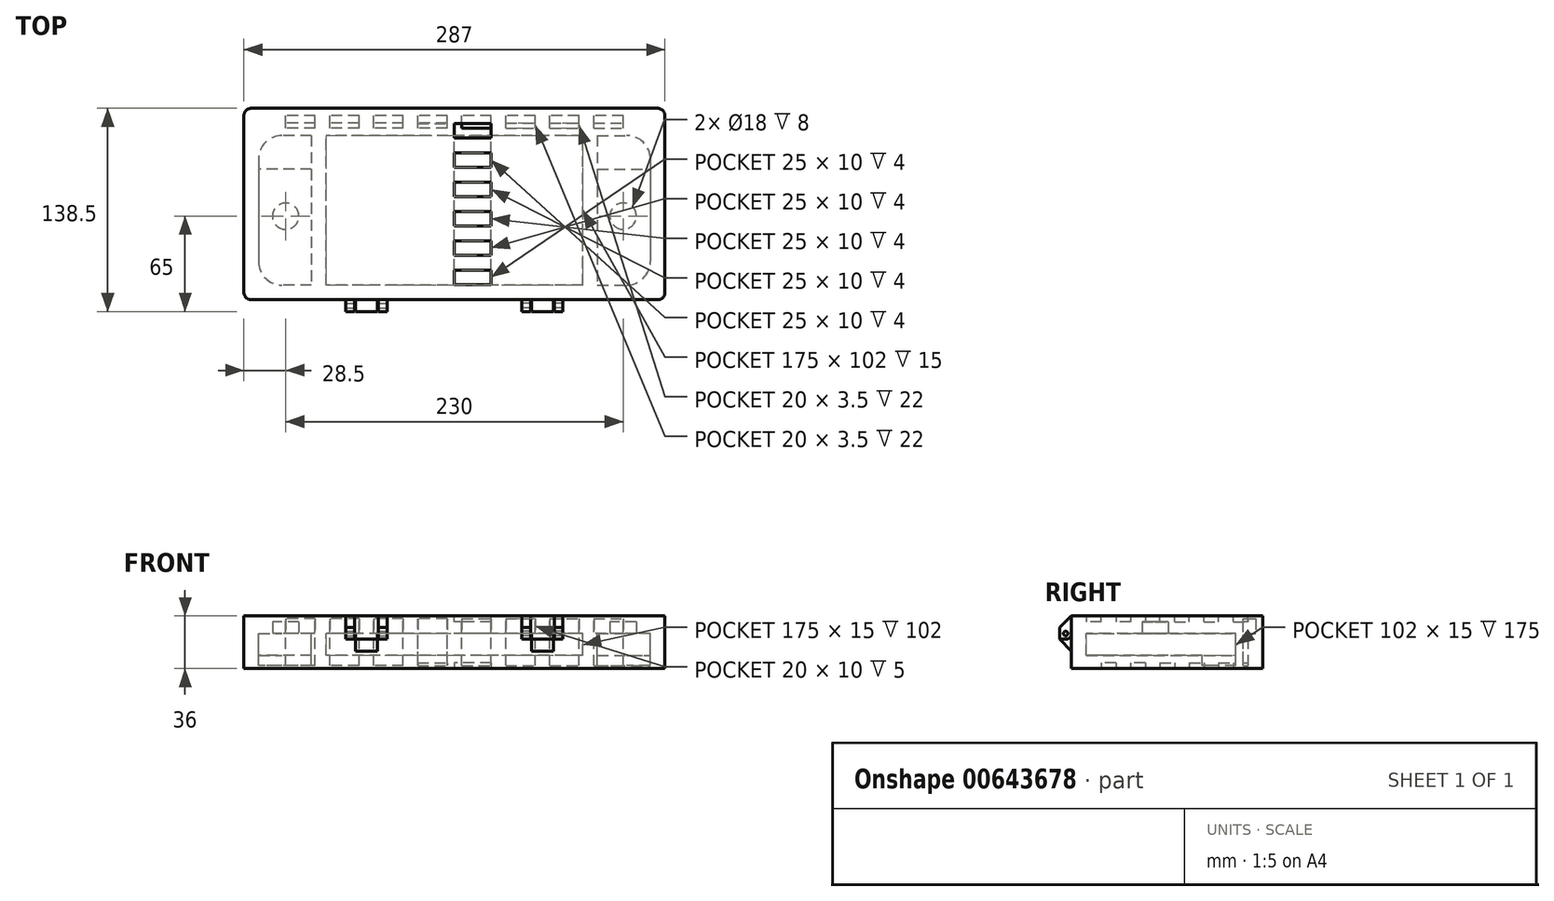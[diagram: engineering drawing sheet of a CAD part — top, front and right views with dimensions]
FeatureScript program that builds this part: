
annotation { "Feature Type Name" : "Feature", "Feature Type Description" : "" }
export const myFeature = defineFeature(function(context is Context, id is Id, definition is map)
    precondition{}
    {
        {
            var Q0;
            Q0=qCreatedBy(makeId("Right.planeOp"),FACE);
            cPlane(context, id + "F0", {"entities" : qUnion([Q0]), "cplaneType" : CPlaneType.OFFSET, "offset" : 60 * mm, "oppositeDirection" : true, "width" : 150 * mm, "height" : 150 * mm});
        }
        {
            var Q0;
            Q0=qCreatedBy(makeId("Right.planeOp"),FACE);
            cPlane(context, id + "F1", {"entities" : qUnion([Q0]), "cplaneType" : CPlaneType.OFFSET, "offset" : 60 * mm, "width" : 150 * mm, "height" : 150 * mm});
        }
        {
            var Q0;
            Q0=qCreatedBy(makeId("Top.planeOp"),FACE);
            var sketch = newSketch(context, id + "F2", { "sketchPlane" : qUnion([Q0])});
            skLineSegment(sketch, "E0.bottom", {"start": v(87.5, -51) * mm, "end": v(-87.5, -51) * mm});
            skLineSegment(sketch, "E0.top", {"start": v(87.5, 51) * mm, "end": v(-87.5, 51) * mm});
            skLineSegment(sketch, "E0.left", {"start": v(87.5, -51) * mm, "end": v(87.5, 51) * mm});
            skLineSegment(sketch, "E0.right", {"start": v(-87.5, -51) * mm, "end": v(-87.5, 51) * mm});
            skPoint(sketch, "E0.middle", {"position": v(0, 0) * mm});
            skLineSegment(sketch, "E1.bottom", {"start": v(97.5, 51) * mm, "end": v(117.5, 51) * mm});
            skLineSegment(sketch, "E1.top", {"start": v(97.5, -51) * mm, "end": v(117.5, -51) * mm});
            skLineSegment(sketch, "E1.left", {"start": v(97.5, 51) * mm, "end": v(97.5, -51) * mm});
            skLineSegment(sketch, "E1.right", {"start": v(133.5, 35) * mm, "end": v(133.5, -35) * mm});
            skPoint(sketch, "E2.visualSharp", {"position": v(133.5, 51) * mm});
            skArc(sketch, "E2.filletArc", {"start": v(133.5, 35) * mm, "mid": v(128.81, 46.31) * mm, "end": v(117.5, 51) * mm});
            skPoint(sketch, "E3.visualSharp", {"position": v(133.5, -51) * mm});
            skArc(sketch, "E3.filletArc", {"start": v(117.5, -51) * mm, "mid": v(128.81, -46.31) * mm, "end": v(133.5, -35) * mm});
            skLineSegment(sketch, "E4.bottom", {"start": v(-97.5, 51) * mm, "end": v(-117.5, 51) * mm});
            skLineSegment(sketch, "E4.top", {"start": v(-97.5, -51) * mm, "end": v(-117.5, -51) * mm});
            skLineSegment(sketch, "E4.left", {"start": v(-97.5, 51) * mm, "end": v(-97.5, -51) * mm});
            skLineSegment(sketch, "E4.right", {"start": v(-133.5, 35) * mm, "end": v(-133.5, -35) * mm});
            skPoint(sketch, "E5.visualSharp", {"position": v(-133.5, 51) * mm});
            skArc(sketch, "E5.filletArc", {"start": v(-117.5, 51) * mm, "mid": v(-128.81, 46.31) * mm, "end": v(-133.5, 35) * mm});
            skPoint(sketch, "E6.visualSharp", {"position": v(-133.5, -51) * mm});
            skArc(sketch, "E6.filletArc", {"start": v(-133.5, -35) * mm, "mid": v(-128.81, -46.31) * mm, "end": v(-117.5, -51) * mm});
            skLineSegment(sketch, "E7.bottom", {"start": v(-143.5, 69.5) * mm, "end": v(143.5, 69.5) * mm, "construction": true});
            skLineSegment(sketch, "E7.top", {"start": v(-143.5, -61) * mm, "end": v(143.5, -61) * mm, "construction": true});
            skLineSegment(sketch, "E7.left", {"start": v(-143.5, 69.5) * mm, "end": v(-143.5, -61) * mm, "construction": true});
            skLineSegment(sketch, "E7.right", {"start": v(143.5, 69.5) * mm, "end": v(143.5, -61) * mm, "construction": true});
            skLineSegment(sketch, "E8.bottom", {"start": v(5, 56) * mm, "end": v(25, 56) * mm});
            skLineSegment(sketch, "E8.top", {"start": v(5, 59.5) * mm, "end": v(25, 59.5) * mm});
            skLineSegment(sketch, "E8.left", {"start": v(5, 56) * mm, "end": v(5, 59.5) * mm});
            skLineSegment(sketch, "E8.right", {"start": v(25, 56) * mm, "end": v(25, 59.5) * mm});
            skLineSegment(sketch, "E9", {"start": v(0, -61) * mm, "end": v(0, 69.5) * mm, "construction": true});
            skLineSegment(sketch, "E10.bottom", {"start": v(35, 56) * mm, "end": v(55, 56) * mm});
            skLineSegment(sketch, "E10.top", {"start": v(35, 59.5) * mm, "end": v(55, 59.5) * mm});
            skLineSegment(sketch, "E10.left", {"start": v(35, 56) * mm, "end": v(35, 59.5) * mm});
            skLineSegment(sketch, "E10.right", {"start": v(55, 56) * mm, "end": v(55, 59.5) * mm});
            skLineSegment(sketch, "E11.bottom", {"start": v(65, 56) * mm, "end": v(85, 56) * mm});
            skLineSegment(sketch, "E11.top", {"start": v(65, 59.5) * mm, "end": v(85, 59.5) * mm});
            skLineSegment(sketch, "E11.left", {"start": v(65, 56) * mm, "end": v(65, 59.5) * mm});
            skLineSegment(sketch, "E11.right", {"start": v(85, 56) * mm, "end": v(85, 59.5) * mm});
            skLineSegment(sketch, "E12.bottom", {"start": v(95, 56) * mm, "end": v(115, 56) * mm});
            skLineSegment(sketch, "E12.top", {"start": v(95, 59.5) * mm, "end": v(115, 59.5) * mm});
            skLineSegment(sketch, "E12.left", {"start": v(95, 56) * mm, "end": v(95, 59.5) * mm});
            skLineSegment(sketch, "E12.right", {"start": v(115, 56) * mm, "end": v(115, 59.5) * mm});
            skLineSegment(sketch, "E13.bottom", {"start": v(-5, 56) * mm, "end": v(-25, 56) * mm});
            skLineSegment(sketch, "E13.top", {"start": v(-5, 59.5) * mm, "end": v(-25, 59.5) * mm});
            skLineSegment(sketch, "E13.left", {"start": v(-5, 56) * mm, "end": v(-5, 59.5) * mm});
            skLineSegment(sketch, "E13.right", {"start": v(-25, 56) * mm, "end": v(-25, 59.5) * mm});
            skLineSegment(sketch, "E14.bottom", {"start": v(-35, 56) * mm, "end": v(-55, 56) * mm});
            skLineSegment(sketch, "E14.top", {"start": v(-35, 59.5) * mm, "end": v(-55, 59.5) * mm});
            skLineSegment(sketch, "E14.left", {"start": v(-35, 56) * mm, "end": v(-35, 59.5) * mm});
            skLineSegment(sketch, "E14.right", {"start": v(-55, 56) * mm, "end": v(-55, 59.5) * mm});
            skLineSegment(sketch, "E15.bottom", {"start": v(-65, 56) * mm, "end": v(-85, 56) * mm});
            skLineSegment(sketch, "E15.top", {"start": v(-65, 59.5) * mm, "end": v(-85, 59.5) * mm});
            skLineSegment(sketch, "E15.left", {"start": v(-65, 56) * mm, "end": v(-65, 59.5) * mm});
            skLineSegment(sketch, "E15.right", {"start": v(-85, 56) * mm, "end": v(-85, 59.5) * mm});
            skLineSegment(sketch, "E16.bottom", {"start": v(-95, 56) * mm, "end": v(-115, 56) * mm});
            skLineSegment(sketch, "E16.top", {"start": v(-95, 59.5) * mm, "end": v(-115, 59.5) * mm});
            skLineSegment(sketch, "E16.left", {"start": v(-95, 56) * mm, "end": v(-95, 59.5) * mm});
            skLineSegment(sketch, "E16.right", {"start": v(-115, 56) * mm, "end": v(-115, 59.5) * mm});
            skLineSegment(sketch, "E17", {"start": v(97.5, 28) * mm, "end": v(133.5, 28) * mm});
            skLineSegment(sketch, "E18", {"start": v(-97.5, 28) * mm, "end": v(-133.5, 28) * mm});
            skPoint(sketch, "E18.startSnap0", {"position": v(115.5, 28) * mm});
            skCircle(sketch, "E19", {"center": v(115, -4) * mm, "radius": 9 * mm});
            skCircle(sketch, "E20", {"center": v(-115, -4) * mm, "radius": 9 * mm});
            skLineSegment(sketch, "E21.bottom", {"start": v(115, 59.5) * mm, "end": v(95, 59.5) * mm});
            skLineSegment(sketch, "E21.top", {"start": v(115, 64.5) * mm, "end": v(95, 64.5) * mm});
            skLineSegment(sketch, "E21.left", {"start": v(115, 59.5) * mm, "end": v(115, 64.5) * mm});
            skLineSegment(sketch, "E21.right", {"start": v(95, 59.5) * mm, "end": v(95, 64.5) * mm});
            skLineSegment(sketch, "E22.bottom", {"start": v(85, 59.5) * mm, "end": v(65, 59.5) * mm});
            skLineSegment(sketch, "E22.top", {"start": v(85, 64.5) * mm, "end": v(65, 64.5) * mm});
            skLineSegment(sketch, "E22.left", {"start": v(85, 59.5) * mm, "end": v(85, 64.5) * mm});
            skLineSegment(sketch, "E22.right", {"start": v(65, 59.5) * mm, "end": v(65, 64.5) * mm});
            skLineSegment(sketch, "E23.bottom", {"start": v(55, 59.5) * mm, "end": v(35, 59.5) * mm});
            skLineSegment(sketch, "E23.top", {"start": v(55, 64.5) * mm, "end": v(35, 64.5) * mm});
            skLineSegment(sketch, "E23.left", {"start": v(55, 59.5) * mm, "end": v(55, 64.5) * mm});
            skLineSegment(sketch, "E23.right", {"start": v(35, 59.5) * mm, "end": v(35, 64.5) * mm});
            skLineSegment(sketch, "E24.bottom", {"start": v(25, 59.5) * mm, "end": v(5, 59.5) * mm});
            skLineSegment(sketch, "E24.top", {"start": v(25, 64.5) * mm, "end": v(5, 64.5) * mm});
            skLineSegment(sketch, "E24.left", {"start": v(25, 59.5) * mm, "end": v(25, 64.5) * mm});
            skLineSegment(sketch, "E24.right", {"start": v(5, 59.5) * mm, "end": v(5, 64.5) * mm});
            skLineSegment(sketch, "E25.top", {"start": v(-5, 64.5) * mm, "end": v(-25, 64.5) * mm});
            skLineSegment(sketch, "E25.left", {"start": v(-5, 59.5) * mm, "end": v(-5, 64.5) * mm});
            skLineSegment(sketch, "E25.right", {"start": v(-25, 59.5) * mm, "end": v(-25, 64.5) * mm});
            skLineSegment(sketch, "E26.top", {"start": v(-35, 64.5) * mm, "end": v(-55, 64.5) * mm});
            skLineSegment(sketch, "E26.left", {"start": v(-35, 59.5) * mm, "end": v(-35, 64.5) * mm});
            skLineSegment(sketch, "E26.right", {"start": v(-55, 59.5) * mm, "end": v(-55, 64.5) * mm});
            skLineSegment(sketch, "E27.top", {"start": v(-65, 64.5) * mm, "end": v(-85, 64.5) * mm});
            skLineSegment(sketch, "E27.left", {"start": v(-65, 59.5) * mm, "end": v(-65, 64.5) * mm});
            skLineSegment(sketch, "E27.right", {"start": v(-85, 59.5) * mm, "end": v(-85, 64.5) * mm});
            skLineSegment(sketch, "E28.top", {"start": v(-95, 64.5) * mm, "end": v(-115, 64.5) * mm});
            skLineSegment(sketch, "E28.left", {"start": v(-95, 59.5) * mm, "end": v(-95, 64.5) * mm});
            skLineSegment(sketch, "E28.right", {"start": v(-115, 59.5) * mm, "end": v(-115, 64.5) * mm});
            skSolve(sketch);
        }
        {
            var Q0;
            Q0=qCreatedBy(makeId("Top.planeOp"),FACE);
            var sketch = newSketch(context, id + "F3", { "sketchPlane" : qUnion([Q0])});
            skLineSegment(sketch, "E29.bottom", {"start": v(138.5, -61) * mm, "end": v(-138.5, -61) * mm});
            skLineSegment(sketch, "E29.top", {"start": v(138.5, 69.5) * mm, "end": v(-138.5, 69.5) * mm});
            skLineSegment(sketch, "E29.left", {"start": v(143.5, -56) * mm, "end": v(143.5, 64.5) * mm});
            skLineSegment(sketch, "E29.right", {"start": v(-143.5, -56) * mm, "end": v(-143.5, 64.5) * mm});
            skPoint(sketch, "E29.middle", {"position": v(0, 0) * mm});
            skLineSegment(sketch, "E30", {"start": v(0, 69.5) * mm, "end": v(0, -61) * mm});
            skPoint(sketch, "E31.visualSharp", {"position": v(-143.5, 69.5) * mm});
            skArc(sketch, "E31.filletArc", {"start": v(-138.5, 69.5) * mm, "mid": v(-142.04, 68.04) * mm, "end": v(-143.5, 64.5) * mm});
            skPoint(sketch, "E32.visualSharp", {"position": v(-143.5, -61) * mm});
            skArc(sketch, "E32.filletArc", {"start": v(-143.5, -56) * mm, "mid": v(-142.04, -59.54) * mm, "end": v(-138.5, -61) * mm});
            skPoint(sketch, "E33.visualSharp", {"position": v(143.5, -61) * mm});
            skArc(sketch, "E33.filletArc", {"start": v(138.5, -61) * mm, "mid": v(142.04, -59.54) * mm, "end": v(143.5, -56) * mm});
            skPoint(sketch, "E34.visualSharp", {"position": v(143.5, 69.5) * mm});
            skArc(sketch, "E34.filletArc", {"start": v(143.5, 64.5) * mm, "mid": v(142.04, 68.04) * mm, "end": v(138.5, 69.5) * mm});
            skSolve(sketch);
        }
        {
            var Q0;
            Q0=qCreatedBy(id+"F0.planeOp",FACE);
            var sketch = newSketch(context, id + "F4", { "sketchPlane" : qUnion([Q0])});
            skLineSegment(sketch, "E35", {"start": v(-61, 65.25) * mm, "end": v(-61, -65.25) * mm, "construction": true});
            skLineSegment(sketch, "E36", {"start": v(-61, 0) * mm, "end": v(-69, 0) * mm});
            skLineSegment(sketch, "E37", {"start": v(-69, 0) * mm, "end": v(-69, -4) * mm});
            skLineSegment(sketch, "E38", {"start": v(-61, 0) * mm, "end": v(-61, -12) * mm});
            skLineSegment(sketch, "E39", {"start": v(-61, -12) * mm, "end": v(-69, -4) * mm});
            skLineSegment(sketch, "E40", {"start": v(-61, 0) * mm, "end": v(-61, 12) * mm});
            skLineSegment(sketch, "E41", {"start": v(-61, 12) * mm, "end": v(-69, 4) * mm});
            skLineSegment(sketch, "E42", {"start": v(-69, 4) * mm, "end": v(-69, 0) * mm});
            skLineSegment(sketch, "E43", {"start": v(-69, 4) * mm, "end": v(-61, 4) * mm});
            skLineSegment(sketch, "E44", {"start": v(-69, -4) * mm, "end": v(-61, -4) * mm});
            skCircle(sketch, "E45", {"center": v(-65, 0) * mm, "radius": 1.5 * mm});
            skPoint(sketch, "E46", {"position": v(-65, -4) * mm});
            skArc(sketch, "E47", {"start": v(-65, 4) * mm, "mid": v(-61, 0) * mm, "end": v(-65, -4) * mm});
            skSolve(sketch);
        }
        {
            var Q0;
            Q0=qCreatedBy(id+"F1.planeOp",FACE);
            var sketch = newSketch(context, id + "F5", { "sketchPlane" : qUnion([Q0])});
            skLineSegment(sketch, "E48", {"start": v(-61, 62.75) * mm, "end": v(-61, -62.75) * mm, "construction": true});
            skLineSegment(sketch, "E49", {"start": v(-61, 0) * mm, "end": v(-69, 0) * mm});
            skLineSegment(sketch, "E50", {"start": v(-69, 0) * mm, "end": v(-69, -4) * mm});
            skLineSegment(sketch, "E51", {"start": v(-61, 0) * mm, "end": v(-61, -12) * mm});
            skLineSegment(sketch, "E52", {"start": v(-61, -12) * mm, "end": v(-69, -4) * mm});
            skLineSegment(sketch, "E53", {"start": v(-61, 0) * mm, "end": v(-61, 12) * mm});
            skLineSegment(sketch, "E54", {"start": v(-61, 12) * mm, "end": v(-69, 4) * mm});
            skLineSegment(sketch, "E55", {"start": v(-69, 4) * mm, "end": v(-69, 0) * mm});
            skLineSegment(sketch, "E56", {"start": v(-69, 4) * mm, "end": v(-61, 4) * mm});
            skLineSegment(sketch, "E57", {"start": v(-69, -4) * mm, "end": v(-61, -4) * mm});
            skCircle(sketch, "E58", {"center": v(-65, 0) * mm, "radius": 1.5 * mm});
            skArc(sketch, "E59", {"start": v(-65, 4) * mm, "mid": v(-61, 0) * mm, "end": v(-65, -4) * mm});
            skSolve(sketch);
        }
        {
            var Q0;
            {var subQ2=sQuery(id+"F3.wireOp",EDGE,"E29.right");Q0=makeQuery(id+"F3.imprint","IMPRINT",FACE,{"disambiguationData":[TD([[makeQuery(id+"F3.imprint","IMPRINT",EDGE,{"derivedFrom":subQ2}),-1.0]])]});}
            extrude(context, id + "F6", {"entities" : qUnion([Q0]), "oppositeDirection" : true, "depth" : 24 * mm, "offsetDistance" : 25 * mm});
        }
        {
            var Q0;
            {var subQ2=sQuery(id+"F3.wireOp",EDGE,"E29.left");Q0=makeQuery(id+"F3.imprint","IMPRINT",FACE,{"disambiguationData":[TD([[makeQuery(id+"F3.imprint","IMPRINT",EDGE,{"derivedFrom":subQ2}),1.0]])]});}
            extrude(context, id + "F7", {"entities" : qUnion([Q0]), "oppositeDirection" : true, "depth" : 24 * mm, "offsetDistance" : 25 * mm});
        }
        {
            var Q0;
            Q0=makeQuery(id+"F3.imprint","IMPRINT",FACE,{"disambiguationData":[TD([[makeQuery(id+"F3.imprint","IMPRINT",EDGE,{"derivedFrom":sQuery(id+"F3.wireOp",EDGE,"E29.right")}),-1.0]])]});
            extrude(context, id + "F8", {"entities" : qUnion([Q0]), "depth" : 12 * mm, "offsetDistance" : 25 * mm});
        }
        {
            var Q0;
            Q0=makeQuery(id+"F3.imprint","IMPRINT",FACE,{"disambiguationData":[TD([[makeQuery(id+"F3.imprint","IMPRINT",EDGE,{"derivedFrom":sQuery(id+"F3.wireOp",EDGE,"E29.left")}),1.0]])]});
            extrude(context, id + "F9", {"entities" : qUnion([Q0]), "depth" : 12 * mm, "offsetDistance" : 25 * mm});
        }
        {
            var Q0;
            {var subQ4=sQuery(id+"F2.wireOp",EDGE,"E4.top");Q0=makeQuery(id+"F2.imprint","IMPRINT",FACE,{"disambiguationData":[TD([[makeQuery(id+"F2.imprint","IMPRINT",EDGE,{"derivedFrom":subQ4}),-1.0]])]});}
            var Q1;
            {var subQ4=sQuery(id+"F2.wireOp",EDGE,"E1.top");Q1=makeQuery(id+"F2.imprint","IMPRINT",FACE,{"disambiguationData":[TD([[makeQuery(id+"F2.imprint","IMPRINT",EDGE,{"derivedFrom":subQ4}),1.0]])]});}
            var Q2;
            Q2=makeQuery(id+"F2.imprint","IMPRINT",FACE,{"disambiguationData":[TD([[makeQuery(id+"F2.imprint","IMPRINT",EDGE,{"derivedFrom":sQuery(id+"F2.wireOp",EDGE,"E0.bottom")}),-1.0]])]});
            var Q3;
            Q3=makeQuery(id+"F2.imprint","IMPRINT",FACE,{"disambiguationData":[TD([[makeQuery(id+"F2.imprint","IMPRINT",EDGE,{"derivedFrom":sQuery(id+"F2.wireOp",EDGE,"E20")}),1.0]])]});
            var Q4;
            Q4=makeQuery(id+"F2.imprint","IMPRINT",FACE,{"disambiguationData":[TD([[makeQuery(id+"F2.imprint","IMPRINT",EDGE,{"derivedFrom":sQuery(id+"F2.wireOp",EDGE,"E19")}),1.0]])]});
            extrude(context, id + "F10", {"entities" : qUnion([Q0, Q1, Q2, Q3, Q4]), "operationType" : NewBodyOperationType.REMOVE, "oppositeDirection" : true, "depth" : 15 * mm, "offsetDistance" : 25 * mm});
        }
        {
            var Q0;
            {var subQ2=sQuery(id+"F2.wireOp",EDGE,"E4.bottom");Q0=makeQuery(id+"F2.imprint","IMPRINT",FACE,{"disambiguationData":[TD([[makeQuery(id+"F2.imprint","IMPRINT",EDGE,{"derivedFrom":subQ2}),1.0]])]});}
            var Q1;
            {var subQ2=sQuery(id+"F2.wireOp",EDGE,"E1.bottom");Q1=makeQuery(id+"F2.imprint","IMPRINT",FACE,{"disambiguationData":[TD([[makeQuery(id+"F2.imprint","IMPRINT",EDGE,{"derivedFrom":subQ2}),-1.0]])]});}
            var Q2;
            Q2=makeQuery(id+"F2.imprint","IMPRINT",FACE,{"disambiguationData":[TD([[makeQuery(id+"F2.imprint","IMPRINT",EDGE,{"derivedFrom":sQuery(id+"F2.wireOp",EDGE,"E16.bottom")}),-1.0]])]});
            var Q3;
            Q3=makeQuery(id+"F2.imprint","IMPRINT",FACE,{"disambiguationData":[TD([[makeQuery(id+"F2.imprint","IMPRINT",EDGE,{"derivedFrom":sQuery(id+"F2.wireOp",EDGE,"E15.bottom")}),-1.0]])]});
            var Q4;
            Q4=makeQuery(id+"F2.imprint","IMPRINT",FACE,{"disambiguationData":[TD([[makeQuery(id+"F2.imprint","IMPRINT",EDGE,{"derivedFrom":sQuery(id+"F2.wireOp",EDGE,"E14.bottom")}),-1.0]])]});
            var Q5;
            Q5=makeQuery(id+"F2.imprint","IMPRINT",FACE,{"disambiguationData":[TD([[makeQuery(id+"F2.imprint","IMPRINT",EDGE,{"derivedFrom":sQuery(id+"F2.wireOp",EDGE,"E13.bottom")}),-1.0]])]});
            var Q6;
            Q6=makeQuery(id+"F2.imprint","IMPRINT",FACE,{"disambiguationData":[TD([[makeQuery(id+"F2.imprint","IMPRINT",EDGE,{"derivedFrom":sQuery(id+"F2.wireOp",EDGE,"E8.bottom")}),1.0]])]});
            var Q7;
            Q7=makeQuery(id+"F2.imprint","IMPRINT",FACE,{"disambiguationData":[TD([[makeQuery(id+"F2.imprint","IMPRINT",EDGE,{"derivedFrom":sQuery(id+"F2.wireOp",EDGE,"E10.bottom")}),1.0]])]});
            var Q8;
            Q8=makeQuery(id+"F2.imprint","IMPRINT",FACE,{"disambiguationData":[TD([[makeQuery(id+"F2.imprint","IMPRINT",EDGE,{"derivedFrom":sQuery(id+"F2.wireOp",EDGE,"E11.bottom")}),1.0]])]});
            var Q9;
            Q9=makeQuery(id+"F2.imprint","IMPRINT",FACE,{"disambiguationData":[TD([[makeQuery(id+"F2.imprint","IMPRINT",EDGE,{"derivedFrom":sQuery(id+"F2.wireOp",EDGE,"E12.bottom")}),1.0]])]});
            extrude(context, id + "F11", {"entities" : qUnion([Q0, Q1, Q2, Q3, Q4, Q5, Q6, Q7, Q8, Q9]), "operationType" : NewBodyOperationType.REMOVE, "oppositeDirection" : true, "depth" : 22 * mm, "offsetDistance" : 25 * mm});
        }
        {
            var Q0;
            Q0=makeQuery(id+"F2.imprint","IMPRINT",FACE,{"disambiguationData":[TD([[makeQuery(id+"F2.imprint","IMPRINT",EDGE,{"derivedFrom":sQuery(id+"F2.wireOp",EDGE,"E16.bottom")}),-1.0]])]});
            var Q1;
            Q1=makeQuery(id+"F2.imprint","IMPRINT",FACE,{"disambiguationData":[TD([[makeQuery(id+"F2.imprint","IMPRINT",EDGE,{"derivedFrom":sQuery(id+"F2.wireOp",EDGE,"E15.bottom")}),-1.0]])]});
            var Q2;
            Q2=makeQuery(id+"F2.imprint","IMPRINT",FACE,{"disambiguationData":[TD([[makeQuery(id+"F2.imprint","IMPRINT",EDGE,{"derivedFrom":sQuery(id+"F2.wireOp",EDGE,"E14.bottom")}),-1.0]])]});
            var Q3;
            Q3=makeQuery(id+"F2.imprint","IMPRINT",FACE,{"disambiguationData":[TD([[makeQuery(id+"F2.imprint","IMPRINT",EDGE,{"derivedFrom":sQuery(id+"F2.wireOp",EDGE,"E13.bottom")}),-1.0]])]});
            var Q4;
            Q4=makeQuery(id+"F2.imprint","IMPRINT",FACE,{"disambiguationData":[TD([[makeQuery(id+"F2.imprint","IMPRINT",EDGE,{"derivedFrom":sQuery(id+"F2.wireOp",EDGE,"E8.bottom")}),1.0]])]});
            var Q5;
            Q5=makeQuery(id+"F2.imprint","IMPRINT",FACE,{"disambiguationData":[TD([[makeQuery(id+"F2.imprint","IMPRINT",EDGE,{"derivedFrom":sQuery(id+"F2.wireOp",EDGE,"E10.bottom")}),1.0]])]});
            var Q6;
            Q6=makeQuery(id+"F2.imprint","IMPRINT",FACE,{"disambiguationData":[TD([[makeQuery(id+"F2.imprint","IMPRINT",EDGE,{"derivedFrom":sQuery(id+"F2.wireOp",EDGE,"E11.bottom")}),1.0]])]});
            var Q7;
            Q7=makeQuery(id+"F2.imprint","IMPRINT",FACE,{"disambiguationData":[TD([[makeQuery(id+"F2.imprint","IMPRINT",EDGE,{"derivedFrom":sQuery(id+"F2.wireOp",EDGE,"E12.bottom")}),1.0]])]});
            var Q8;
            Q8=makeQuery(id+"F2.imprint","IMPRINT",FACE,{"disambiguationData":[TD([[makeQuery(id+"F2.imprint","IMPRINT",EDGE,{"derivedFrom":sQuery(id+"F2.wireOp",EDGE,"E12.top")}),1.0]])]});
            var Q9;
            Q9=makeQuery(id+"F2.imprint","IMPRINT",FACE,{"disambiguationData":[TD([[makeQuery(id+"F2.imprint","IMPRINT",EDGE,{"derivedFrom":sQuery(id+"F2.wireOp",EDGE,"E11.top")}),1.0]])]});
            var Q10;
            Q10=makeQuery(id+"F2.imprint","IMPRINT",FACE,{"disambiguationData":[TD([[makeQuery(id+"F2.imprint","IMPRINT",EDGE,{"derivedFrom":sQuery(id+"F2.wireOp",EDGE,"E10.top")}),1.0]])]});
            var Q11;
            Q11=makeQuery(id+"F2.imprint","IMPRINT",FACE,{"disambiguationData":[TD([[makeQuery(id+"F2.imprint","IMPRINT",EDGE,{"derivedFrom":sQuery(id+"F2.wireOp",EDGE,"E8.top")}),1.0]])]});
            var Q12;
            Q12=makeQuery(id+"F2.imprint","IMPRINT",FACE,{"disambiguationData":[TD([[makeQuery(id+"F2.imprint","IMPRINT",EDGE,{"derivedFrom":sQuery(id+"F2.wireOp",EDGE,"E13.top")}),-1.0]])]});
            var Q13;
            Q13=makeQuery(id+"F2.imprint","IMPRINT",FACE,{"disambiguationData":[TD([[makeQuery(id+"F2.imprint","IMPRINT",EDGE,{"derivedFrom":sQuery(id+"F2.wireOp",EDGE,"E14.top")}),-1.0]])]});
            var Q14;
            Q14=makeQuery(id+"F2.imprint","IMPRINT",FACE,{"disambiguationData":[TD([[makeQuery(id+"F2.imprint","IMPRINT",EDGE,{"derivedFrom":sQuery(id+"F2.wireOp",EDGE,"E15.top")}),-1.0]])]});
            var Q15;
            Q15=makeQuery(id+"F2.imprint","IMPRINT",FACE,{"disambiguationData":[TD([[makeQuery(id+"F2.imprint","IMPRINT",EDGE,{"derivedFrom":sQuery(id+"F2.wireOp",EDGE,"E16.top")}),-1.0]])]});
            extrude(context, id + "F12", {"entities" : qUnion([Q0, Q1, Q2, Q3, Q4, Q5, Q6, Q7, Q8, Q9, Q10, Q11, Q12, Q13, Q14, Q15]), "operationType" : NewBodyOperationType.REMOVE, "depth" : 10 * mm, "offsetDistance" : 25 * mm});
        }
        {
            var Q0;
            Q0=makeQuery(id+"F2.imprint","IMPRINT",FACE,{"disambiguationData":[TD([[makeQuery(id+"F2.imprint","IMPRINT",EDGE,{"derivedFrom":sQuery(id+"F2.wireOp",EDGE,"E20")}),1.0]])]});
            var Q1;
            Q1=makeQuery(id+"F2.imprint","IMPRINT",FACE,{"disambiguationData":[TD([[makeQuery(id+"F2.imprint","IMPRINT",EDGE,{"derivedFrom":sQuery(id+"F2.wireOp",EDGE,"E19")}),1.0]])]});
            extrude(context, id + "F13", {"entities" : qUnion([Q0, Q1]), "operationType" : NewBodyOperationType.REMOVE, "depth" : 8 * mm, "offsetDistance" : 25 * mm});
        }
        {
            var Q0;
            {var subQ2=sQuery(id+"F4.wireOp",EDGE,"E39");Q0=makeQuery(id+"F4.imprint","IMPRINT",FACE,{"disambiguationData":[TD([[makeQuery(id+"F4.imprint","IMPRINT",EDGE,{"derivedFrom":subQ2}),-1.0]])]});}
            var Q1;
            {var subQ4=sQuery(id+"F4.wireOp",EDGE,"E37");Q1=makeQuery(id+"F4.imprint","IMPRINT",FACE,{"disambiguationData":[TD([[makeQuery(id+"F4.imprint","IMPRINT",EDGE,{"derivedFrom":subQ4}),1.0]])]});}
            var Q2;
            {var subQ0=sQuery(id+"F4.wireOp",EDGE,"E42");Q2=makeQuery(id+"F4.imprint","IMPRINT",FACE,{"disambiguationData":[TD([[makeQuery(id+"F4.imprint","IMPRINT",EDGE,{"derivedFrom":subQ0}),1.0]])]});}
            var Q3;
            {var subQ0=sQuery(id+"F4.wireOp",EDGE,"E44");var subQ1=sQuery(id+"F4.wireOp",EDGE,"E38");var subQ2=makeQuery(id+"F4.imprint","INTERSECT",VERTEX,{"derivedFrom":[subQ1,subQ0]});Q3=makeQuery(id+"F4.imprint","IMPRINT",FACE,{"disambiguationData":[TD([[makeQuery(id+"F4.imprint","IMPRINT",EDGE,{"disambiguationData":[TD([[subQ2,1.0]])],"derivedFrom":subQ0}),1.0]])]});}
            extrude(context, id + "F14", {"entities" : qUnion([Q0, Q1, Q2, Q3]), "operationType" : NewBodyOperationType.ADD, "endBound" : BoundingType.SYMMETRIC, "oppositeDirection" : true, "depth" : 15 * mm, "offsetDistance" : 25 * mm});
        }
        {
            var Q0;
            {var subQ2=sQuery(id+"F5.wireOp",EDGE,"E52");Q0=makeQuery(id+"F5.imprint","IMPRINT",FACE,{"disambiguationData":[TD([[makeQuery(id+"F5.imprint","IMPRINT",EDGE,{"derivedFrom":subQ2}),-1.0]])]});}
            var Q1;
            {var subQ4=sQuery(id+"F5.wireOp",EDGE,"E50");Q1=makeQuery(id+"F5.imprint","IMPRINT",FACE,{"disambiguationData":[TD([[makeQuery(id+"F5.imprint","IMPRINT",EDGE,{"derivedFrom":subQ4}),1.0]])]});}
            var Q2;
            {var subQ0=sQuery(id+"F5.wireOp",EDGE,"E55");Q2=makeQuery(id+"F5.imprint","IMPRINT",FACE,{"disambiguationData":[TD([[makeQuery(id+"F5.imprint","IMPRINT",EDGE,{"derivedFrom":subQ0}),1.0]])]});}
            var Q3;
            {var subQ0=sQuery(id+"F5.wireOp",EDGE,"E57");var subQ1=sQuery(id+"F5.wireOp",EDGE,"E51");var subQ2=makeQuery(id+"F5.imprint","INTERSECT",VERTEX,{"derivedFrom":[subQ1,subQ0]});Q3=makeQuery(id+"F5.imprint","IMPRINT",FACE,{"disambiguationData":[TD([[makeQuery(id+"F5.imprint","IMPRINT",EDGE,{"disambiguationData":[TD([[subQ2,1.0]])],"derivedFrom":subQ0}),1.0]])]});}
            extrude(context, id + "F15", {"entities" : qUnion([Q0, Q1, Q2, Q3]), "operationType" : NewBodyOperationType.ADD, "endBound" : BoundingType.SYMMETRIC, "depth" : 15 * mm, "offsetDistance" : 25 * mm});
        }
        {
            var Q0;
            {var subQ4=sQuery(id+"F4.wireOp",EDGE,"E37");Q0=makeQuery(id+"F4.imprint","IMPRINT",FACE,{"disambiguationData":[TD([[makeQuery(id+"F4.imprint","IMPRINT",EDGE,{"derivedFrom":subQ4}),1.0]])]});}
            var Q1;
            {var subQ0=sQuery(id+"F4.wireOp",EDGE,"E42");Q1=makeQuery(id+"F4.imprint","IMPRINT",FACE,{"disambiguationData":[TD([[makeQuery(id+"F4.imprint","IMPRINT",EDGE,{"derivedFrom":subQ0}),1.0]])]});}
            var Q2;
            {var subQ2=sQuery(id+"F4.wireOp",EDGE,"E41");Q2=makeQuery(id+"F4.imprint","IMPRINT",FACE,{"disambiguationData":[TD([[makeQuery(id+"F4.imprint","IMPRINT",EDGE,{"derivedFrom":subQ2}),1.0]])]});}
            var Q3;
            {var subQ0=sQuery(id+"F4.wireOp",EDGE,"E43");var subQ1=sQuery(id+"F4.wireOp",EDGE,"E40");var subQ2=makeQuery(id+"F4.imprint","INTERSECT",VERTEX,{"derivedFrom":[subQ1,subQ0]});Q3=makeQuery(id+"F4.imprint","IMPRINT",FACE,{"disambiguationData":[TD([[makeQuery(id+"F4.imprint","IMPRINT",EDGE,{"disambiguationData":[TD([[subQ2,1.0]])],"derivedFrom":subQ0}),-1.0]])]});}
            extrude(context, id + "F16", {"entities" : qUnion([Q0, Q1, Q2, Q3]), "operationType" : NewBodyOperationType.ADD, "endBound" : BoundingType.SYMMETRIC, "depth" : 28 * mm, "offsetDistance" : 25 * mm});
        }
        {
            var Q0;
            {var subQ4=sQuery(id+"F4.wireOp",EDGE,"E37");Q0=makeQuery(id+"F4.imprint","IMPRINT",FACE,{"disambiguationData":[TD([[makeQuery(id+"F4.imprint","IMPRINT",EDGE,{"derivedFrom":subQ4}),1.0]])]});}
            var Q1;
            {var subQ0=sQuery(id+"F4.wireOp",EDGE,"E42");Q1=makeQuery(id+"F4.imprint","IMPRINT",FACE,{"disambiguationData":[TD([[makeQuery(id+"F4.imprint","IMPRINT",EDGE,{"derivedFrom":subQ0}),1.0]])]});}
            var Q2;
            {var subQ2=sQuery(id+"F4.wireOp",EDGE,"E41");Q2=makeQuery(id+"F4.imprint","IMPRINT",FACE,{"disambiguationData":[TD([[makeQuery(id+"F4.imprint","IMPRINT",EDGE,{"derivedFrom":subQ2}),1.0]])]});}
            var Q3;
            {var subQ0=sQuery(id+"F4.wireOp",EDGE,"E43");var subQ1=sQuery(id+"F4.wireOp",EDGE,"E40");var subQ2=makeQuery(id+"F4.imprint","INTERSECT",VERTEX,{"derivedFrom":[subQ1,subQ0]});Q3=makeQuery(id+"F4.imprint","IMPRINT",FACE,{"disambiguationData":[TD([[makeQuery(id+"F4.imprint","IMPRINT",EDGE,{"disambiguationData":[TD([[subQ2,1.0]])],"derivedFrom":subQ0}),-1.0]])]});}
            extrude(context, id + "F17", {"entities" : qUnion([Q0, Q1, Q2, Q3]), "operationType" : NewBodyOperationType.REMOVE, "endBound" : BoundingType.SYMMETRIC, "depth" : 16 * mm, "offsetDistance" : 25 * mm});
        }
        {
            var Q0;
            {var subQ4=sQuery(id+"F5.wireOp",EDGE,"E50");Q0=makeQuery(id+"F5.imprint","IMPRINT",FACE,{"disambiguationData":[TD([[makeQuery(id+"F5.imprint","IMPRINT",EDGE,{"derivedFrom":subQ4}),1.0]])]});}
            var Q1;
            {var subQ0=sQuery(id+"F5.wireOp",EDGE,"E55");Q1=makeQuery(id+"F5.imprint","IMPRINT",FACE,{"disambiguationData":[TD([[makeQuery(id+"F5.imprint","IMPRINT",EDGE,{"derivedFrom":subQ0}),1.0]])]});}
            var Q2;
            {var subQ2=sQuery(id+"F5.wireOp",EDGE,"E54");Q2=makeQuery(id+"F5.imprint","IMPRINT",FACE,{"disambiguationData":[TD([[makeQuery(id+"F5.imprint","IMPRINT",EDGE,{"derivedFrom":subQ2}),1.0]])]});}
            var Q3;
            {var subQ0=sQuery(id+"F5.wireOp",EDGE,"E56");var subQ1=sQuery(id+"F5.wireOp",EDGE,"E53");var subQ2=makeQuery(id+"F5.imprint","INTERSECT",VERTEX,{"derivedFrom":[subQ1,subQ0]});Q3=makeQuery(id+"F5.imprint","IMPRINT",FACE,{"disambiguationData":[TD([[makeQuery(id+"F5.imprint","IMPRINT",EDGE,{"disambiguationData":[TD([[subQ2,1.0]])],"derivedFrom":subQ0}),-1.0]])]});}
            extrude(context, id + "F18", {"entities" : qUnion([Q0, Q1, Q2, Q3]), "operationType" : NewBodyOperationType.ADD, "endBound" : BoundingType.SYMMETRIC, "depth" : 28 * mm, "offsetDistance" : 25 * mm});
        }
        {
            var Q0;
            {var subQ4=sQuery(id+"F5.wireOp",EDGE,"E50");Q0=makeQuery(id+"F5.imprint","IMPRINT",FACE,{"disambiguationData":[TD([[makeQuery(id+"F5.imprint","IMPRINT",EDGE,{"derivedFrom":subQ4}),1.0]])]});}
            var Q1;
            {var subQ0=sQuery(id+"F5.wireOp",EDGE,"E55");Q1=makeQuery(id+"F5.imprint","IMPRINT",FACE,{"disambiguationData":[TD([[makeQuery(id+"F5.imprint","IMPRINT",EDGE,{"derivedFrom":subQ0}),1.0]])]});}
            var Q2;
            {var subQ2=sQuery(id+"F5.wireOp",EDGE,"E54");Q2=makeQuery(id+"F5.imprint","IMPRINT",FACE,{"disambiguationData":[TD([[makeQuery(id+"F5.imprint","IMPRINT",EDGE,{"derivedFrom":subQ2}),1.0]])]});}
            var Q3;
            {var subQ0=sQuery(id+"F5.wireOp",EDGE,"E56");var subQ1=sQuery(id+"F5.wireOp",EDGE,"E53");var subQ2=makeQuery(id+"F5.imprint","INTERSECT",VERTEX,{"derivedFrom":[subQ1,subQ0]});Q3=makeQuery(id+"F5.imprint","IMPRINT",FACE,{"disambiguationData":[TD([[makeQuery(id+"F5.imprint","IMPRINT",EDGE,{"disambiguationData":[TD([[subQ2,1.0]])],"derivedFrom":subQ0}),-1.0]])]});}
            extrude(context, id + "F19", {"entities" : qUnion([Q0, Q1, Q2, Q3]), "operationType" : NewBodyOperationType.REMOVE, "endBound" : BoundingType.SYMMETRIC, "oppositeDirection" : true, "depth" : 16 * mm, "offsetDistance" : 25 * mm});
        }
        {
            var Q0;
            Q0=qCreatedBy(makeId("Right.planeOp"),FACE);
            var sketch = newSketch(context, id + "F20", { "sketchPlane" : qUnion([Q0])});
            skLineSegment(sketch, "E60.bottom", {"start": v(-61, 12) * mm, "end": v(69.5, 12) * mm});
            skLineSegment(sketch, "E60.top", {"start": v(-61, -24) * mm, "end": v(69.5, -24) * mm});
            skLineSegment(sketch, "E60.left", {"start": v(-61, 12) * mm, "end": v(-61, -24) * mm});
            skLineSegment(sketch, "E60.right", {"start": v(69.5, 12) * mm, "end": v(69.5, -24) * mm});
            skPoint(sketch, "E61", {"position": v(4.25, 12) * mm});
            skPoint(sketch, "E62", {"position": v(4.25, -24) * mm});
            skLineSegment(sketch, "E63", {"start": v(4.25, 12) * mm, "end": v(4.25, -24) * mm});
            skLineSegment(sketch, "E64", {"start": v(9.25, 8) * mm, "end": v(-0.75, 8) * mm});
            skPoint(sketch, "E65", {"position": v(4.25, 8) * mm});
            skLineSegment(sketch, "E66", {"start": v(-0.75, -20) * mm, "end": v(9.25, -20) * mm});
            skLineSegment(sketch, "E67", {"start": v(9.25, 8) * mm, "end": v(9.25, 12) * mm});
            skLineSegment(sketch, "E68", {"start": v(-0.75, 8) * mm, "end": v(-0.75, 12) * mm});
            skLineSegment(sketch, "E69", {"start": v(9.25, -20) * mm, "end": v(9.25, -24) * mm});
            skLineSegment(sketch, "E70", {"start": v(-0.75, -20) * mm, "end": v(-0.75, -24) * mm});
            skLineSegment(sketch, "E71", {"start": v(9.25, 8) * mm, "end": v(69.5, 8) * mm});
            skLineSegment(sketch, "E72", {"start": v(9.25, -20) * mm, "end": v(69.5, -20) * mm});
            skLineSegment(sketch, "E73", {"start": v(-0.75, 8) * mm, "end": v(-61, 8) * mm});
            skLineSegment(sketch, "E74", {"start": v(-0.75, -20) * mm, "end": v(-61, -20) * mm});
            skLineSegment(sketch, "E75", {"start": v(19.25, 8) * mm, "end": v(19.25, 12) * mm});
            skLineSegment(sketch, "E76", {"start": v(29.25, 8) * mm, "end": v(29.25, 12) * mm});
            skLineSegment(sketch, "E77", {"start": v(39.25, 8) * mm, "end": v(39.25, 12) * mm});
            skLineSegment(sketch, "E78", {"start": v(49.25, 8) * mm, "end": v(49.25, 12) * mm});
            skLineSegment(sketch, "E79", {"start": v(59.25, 8) * mm, "end": v(59.25, 12) * mm});
            skLineSegment(sketch, "E80", {"start": v(-10.75, 12) * mm, "end": v(-10.75, 8) * mm});
            skLineSegment(sketch, "E81", {"start": v(-20.75, 12) * mm, "end": v(-20.75, 8) * mm});
            skLineSegment(sketch, "E82", {"start": v(-30.75, 12) * mm, "end": v(-30.75, 8) * mm});
            skLineSegment(sketch, "E83", {"start": v(-40.75, 8) * mm, "end": v(-40.75, 12) * mm});
            skLineSegment(sketch, "E84", {"start": v(-50.75, 8) * mm, "end": v(-50.75, 12) * mm});
            skLineSegment(sketch, "E85", {"start": v(19.25, -20) * mm, "end": v(19.25, -24) * mm});
            skLineSegment(sketch, "E86", {"start": v(29.25, -20) * mm, "end": v(29.25, -24) * mm});
            skLineSegment(sketch, "E87", {"start": v(39.25, -20) * mm, "end": v(39.25, -24) * mm});
            skLineSegment(sketch, "E88", {"start": v(49.25, -20) * mm, "end": v(49.25, -24) * mm});
            skLineSegment(sketch, "E89", {"start": v(59.25, -20) * mm, "end": v(59.25, -24) * mm});
            skLineSegment(sketch, "E90", {"start": v(-10.75, -20) * mm, "end": v(-10.75, -24) * mm});
            skLineSegment(sketch, "E91", {"start": v(-20.75, -20) * mm, "end": v(-20.75, -24) * mm});
            skLineSegment(sketch, "E92", {"start": v(-30.75, -20) * mm, "end": v(-30.75, -24) * mm});
            skLineSegment(sketch, "E93", {"start": v(-40.75, -20) * mm, "end": v(-40.75, -24) * mm});
            skLineSegment(sketch, "E94", {"start": v(-50.75, -20) * mm, "end": v(-50.75, -24) * mm});
            skSolve(sketch);
        }
        {
            var Q0;
            {var subQ0=sQuery(id+"F20.wireOp",EDGE,"E83");Q0=makeQuery(id+"F20.imprint","IMPRINT",FACE,{"disambiguationData":[TD([[makeQuery(id+"F20.imprint","IMPRINT",EDGE,{"derivedFrom":subQ0}),1.0]])]});}
            var Q1;
            {var subQ0=sQuery(id+"F20.wireOp",EDGE,"E81");Q1=makeQuery(id+"F20.imprint","IMPRINT",FACE,{"disambiguationData":[TD([[makeQuery(id+"F20.imprint","IMPRINT",EDGE,{"derivedFrom":subQ0}),-1.0]])]});}
            var Q2;
            {var subQ0=sQuery(id+"F20.wireOp",EDGE,"E68");Q2=makeQuery(id+"F20.imprint","IMPRINT",FACE,{"disambiguationData":[TD([[makeQuery(id+"F20.imprint","IMPRINT",EDGE,{"derivedFrom":subQ0}),1.0]])]});}
            var Q3;
            {var subQ0=sQuery(id+"F20.wireOp",EDGE,"E67");Q3=makeQuery(id+"F20.imprint","IMPRINT",FACE,{"disambiguationData":[TD([[makeQuery(id+"F20.imprint","IMPRINT",EDGE,{"derivedFrom":subQ0}),-1.0]])]});}
            var Q4;
            {var subQ0=sQuery(id+"F20.wireOp",EDGE,"E76");Q4=makeQuery(id+"F20.imprint","IMPRINT",FACE,{"disambiguationData":[TD([[makeQuery(id+"F20.imprint","IMPRINT",EDGE,{"derivedFrom":subQ0}),-1.0]])]});}
            var Q5;
            {var subQ0=sQuery(id+"F20.wireOp",EDGE,"E78");Q5=makeQuery(id+"F20.imprint","IMPRINT",FACE,{"disambiguationData":[TD([[makeQuery(id+"F20.imprint","IMPRINT",EDGE,{"derivedFrom":subQ0}),-1.0]])]});}
            extrude(context, id + "F21", {"entities" : qUnion([Q0, Q1, Q2, Q3, Q4, Q5]), "operationType" : NewBodyOperationType.ADD, "depth" : 25 * mm, "offsetDistance" : 25 * mm});
        }
        {
            var Q0;
            {var subQ0=sQuery(id+"F20.wireOp",EDGE,"E82");Q0=makeQuery(id+"F20.imprint","IMPRINT",FACE,{"disambiguationData":[TD([[makeQuery(id+"F20.imprint","IMPRINT",EDGE,{"derivedFrom":subQ0}),-1.0]])]});}
            var Q1;
            {var subQ0=sQuery(id+"F20.wireOp",EDGE,"E80");Q1=makeQuery(id+"F20.imprint","IMPRINT",FACE,{"disambiguationData":[TD([[makeQuery(id+"F20.imprint","IMPRINT",EDGE,{"derivedFrom":subQ0}),-1.0]])]});}
            var Q2;
            {var subQ3=sQuery(id+"F20.wireOp",EDGE,"E67");Q2=makeQuery(id+"F20.imprint","IMPRINT",FACE,{"disambiguationData":[TD([[makeQuery(id+"F20.imprint","IMPRINT",EDGE,{"derivedFrom":subQ3}),1.0]])]});}
            var Q3;
            {var subQ3=sQuery(id+"F20.wireOp",EDGE,"E68");Q3=makeQuery(id+"F20.imprint","IMPRINT",FACE,{"disambiguationData":[TD([[makeQuery(id+"F20.imprint","IMPRINT",EDGE,{"derivedFrom":subQ3}),-1.0]])]});}
            var Q4;
            {var subQ2=sQuery(id+"F20.wireOp",EDGE,"E75");Q4=makeQuery(id+"F20.imprint","IMPRINT",FACE,{"disambiguationData":[TD([[makeQuery(id+"F20.imprint","IMPRINT",EDGE,{"derivedFrom":subQ2}),-1.0]])]});}
            var Q5;
            {var subQ0=sQuery(id+"F20.wireOp",EDGE,"E77");Q5=makeQuery(id+"F20.imprint","IMPRINT",FACE,{"disambiguationData":[TD([[makeQuery(id+"F20.imprint","IMPRINT",EDGE,{"derivedFrom":subQ0}),-1.0]])]});}
            extrude(context, id + "F22", {"entities" : qUnion([Q0, Q1, Q2, Q3, Q4, Q5]), "operationType" : NewBodyOperationType.REMOVE, "oppositeDirection" : true, "depth" : 25 * mm, "offsetDistance" : 25 * mm});
        }
        {
            var Q0;
            {var subQ2=sQuery(id+"F20.wireOp",EDGE,"E92");Q0=makeQuery(id+"F20.imprint","IMPRINT",FACE,{"disambiguationData":[TD([[makeQuery(id+"F20.imprint","IMPRINT",EDGE,{"derivedFrom":subQ2}),-1.0]])]});}
            var Q1;
            {var subQ0=sQuery(id+"F20.wireOp",EDGE,"E90");Q1=makeQuery(id+"F20.imprint","IMPRINT",FACE,{"disambiguationData":[TD([[makeQuery(id+"F20.imprint","IMPRINT",EDGE,{"derivedFrom":subQ0}),-1.0]])]});}
            var Q2;
            {var subQ3=sQuery(id+"F20.wireOp",EDGE,"E69");Q2=makeQuery(id+"F20.imprint","IMPRINT",FACE,{"disambiguationData":[TD([[makeQuery(id+"F20.imprint","IMPRINT",EDGE,{"derivedFrom":subQ3}),-1.0]])]});}
            var Q3;
            {var subQ3=sQuery(id+"F20.wireOp",EDGE,"E70");Q3=makeQuery(id+"F20.imprint","IMPRINT",FACE,{"disambiguationData":[TD([[makeQuery(id+"F20.imprint","IMPRINT",EDGE,{"derivedFrom":subQ3}),1.0]])]});}
            var Q4;
            {var subQ0=sQuery(id+"F20.wireOp",EDGE,"E85");Q4=makeQuery(id+"F20.imprint","IMPRINT",FACE,{"disambiguationData":[TD([[makeQuery(id+"F20.imprint","IMPRINT",EDGE,{"derivedFrom":subQ0}),1.0]])]});}
            var Q5;
            {var subQ0=sQuery(id+"F20.wireOp",EDGE,"E87");Q5=makeQuery(id+"F20.imprint","IMPRINT",FACE,{"disambiguationData":[TD([[makeQuery(id+"F20.imprint","IMPRINT",EDGE,{"derivedFrom":subQ0}),1.0]])]});}
            extrude(context, id + "F23", {"entities" : qUnion([Q0, Q1, Q2, Q3, Q4, Q5]), "operationType" : NewBodyOperationType.ADD, "depth" : 25 * mm, "offsetDistance" : 25 * mm});
        }
        {
            var Q0;
            {var subQ0=sQuery(id+"F20.wireOp",EDGE,"E93");Q0=makeQuery(id+"F20.imprint","IMPRINT",FACE,{"disambiguationData":[TD([[makeQuery(id+"F20.imprint","IMPRINT",EDGE,{"derivedFrom":subQ0}),-1.0]])]});}
            var Q1;
            {var subQ0=sQuery(id+"F20.wireOp",EDGE,"E91");Q1=makeQuery(id+"F20.imprint","IMPRINT",FACE,{"disambiguationData":[TD([[makeQuery(id+"F20.imprint","IMPRINT",EDGE,{"derivedFrom":subQ0}),-1.0]])]});}
            var Q2;
            {var subQ0=sQuery(id+"F20.wireOp",EDGE,"E70");Q2=makeQuery(id+"F20.imprint","IMPRINT",FACE,{"disambiguationData":[TD([[makeQuery(id+"F20.imprint","IMPRINT",EDGE,{"derivedFrom":subQ0}),-1.0]])]});}
            var Q3;
            {var subQ0=sQuery(id+"F20.wireOp",EDGE,"E69");Q3=makeQuery(id+"F20.imprint","IMPRINT",FACE,{"disambiguationData":[TD([[makeQuery(id+"F20.imprint","IMPRINT",EDGE,{"derivedFrom":subQ0}),1.0]])]});}
            var Q4;
            {var subQ0=sQuery(id+"F20.wireOp",EDGE,"E86");Q4=makeQuery(id+"F20.imprint","IMPRINT",FACE,{"disambiguationData":[TD([[makeQuery(id+"F20.imprint","IMPRINT",EDGE,{"derivedFrom":subQ0}),1.0]])]});}
            var Q5;
            {var subQ0=sQuery(id+"F20.wireOp",EDGE,"E88");Q5=makeQuery(id+"F20.imprint","IMPRINT",FACE,{"disambiguationData":[TD([[makeQuery(id+"F20.imprint","IMPRINT",EDGE,{"derivedFrom":subQ0}),1.0]])]});}
            extrude(context, id + "F24", {"entities" : qUnion([Q0, Q1, Q2, Q3, Q4, Q5]), "operationType" : NewBodyOperationType.REMOVE, "oppositeDirection" : true, "depth" : 25 * mm, "offsetDistance" : 25 * mm});
        }
        {
            var Q0;
            {var subQ0=sQuery(id+"F20.wireOp",EDGE,"E93");Q0=makeQuery(id+"F20.imprint","IMPRINT",FACE,{"disambiguationData":[TD([[makeQuery(id+"F20.imprint","IMPRINT",EDGE,{"derivedFrom":subQ0}),-1.0]])]});}
            var Q1;
            {var subQ0=sQuery(id+"F20.wireOp",EDGE,"E91");Q1=makeQuery(id+"F20.imprint","IMPRINT",FACE,{"disambiguationData":[TD([[makeQuery(id+"F20.imprint","IMPRINT",EDGE,{"derivedFrom":subQ0}),-1.0]])]});}
            var Q2;
            {var subQ0=sQuery(id+"F20.wireOp",EDGE,"E70");Q2=makeQuery(id+"F20.imprint","IMPRINT",FACE,{"disambiguationData":[TD([[makeQuery(id+"F20.imprint","IMPRINT",EDGE,{"derivedFrom":subQ0}),-1.0]])]});}
            var Q3;
            {var subQ0=sQuery(id+"F20.wireOp",EDGE,"E69");Q3=makeQuery(id+"F20.imprint","IMPRINT",FACE,{"disambiguationData":[TD([[makeQuery(id+"F20.imprint","IMPRINT",EDGE,{"derivedFrom":subQ0}),1.0]])]});}
            var Q4;
            {var subQ0=sQuery(id+"F20.wireOp",EDGE,"E86");Q4=makeQuery(id+"F20.imprint","IMPRINT",FACE,{"disambiguationData":[TD([[makeQuery(id+"F20.imprint","IMPRINT",EDGE,{"derivedFrom":subQ0}),1.0]])]});}
            var Q5;
            {var subQ0=sQuery(id+"F20.wireOp",EDGE,"E88");Q5=makeQuery(id+"F20.imprint","IMPRINT",FACE,{"disambiguationData":[TD([[makeQuery(id+"F20.imprint","IMPRINT",EDGE,{"derivedFrom":subQ0}),1.0]])]});}
            extrude(context, id + "F25", {"entities" : qUnion([Q0, Q1, Q2, Q3, Q4, Q5]), "operationType" : NewBodyOperationType.ADD, "oppositeDirection" : true, "depth" : 25 * mm, "offsetDistance" : 25 * mm});
        }
        {
            var Q0;
            {var subQ0=sQuery(id+"F20.wireOp",EDGE,"E87");Q0=makeQuery(id+"F20.imprint","IMPRINT",FACE,{"disambiguationData":[TD([[makeQuery(id+"F20.imprint","IMPRINT",EDGE,{"derivedFrom":subQ0}),1.0]])]});}
            var Q1;
            {var subQ0=sQuery(id+"F20.wireOp",EDGE,"E85");Q1=makeQuery(id+"F20.imprint","IMPRINT",FACE,{"disambiguationData":[TD([[makeQuery(id+"F20.imprint","IMPRINT",EDGE,{"derivedFrom":subQ0}),1.0]])]});}
            var Q2;
            {var subQ3=sQuery(id+"F20.wireOp",EDGE,"E70");Q2=makeQuery(id+"F20.imprint","IMPRINT",FACE,{"disambiguationData":[TD([[makeQuery(id+"F20.imprint","IMPRINT",EDGE,{"derivedFrom":subQ3}),1.0]])]});}
            var Q3;
            {var subQ3=sQuery(id+"F20.wireOp",EDGE,"E69");Q3=makeQuery(id+"F20.imprint","IMPRINT",FACE,{"disambiguationData":[TD([[makeQuery(id+"F20.imprint","IMPRINT",EDGE,{"derivedFrom":subQ3}),-1.0]])]});}
            var Q4;
            {var subQ0=sQuery(id+"F20.wireOp",EDGE,"E90");Q4=makeQuery(id+"F20.imprint","IMPRINT",FACE,{"disambiguationData":[TD([[makeQuery(id+"F20.imprint","IMPRINT",EDGE,{"derivedFrom":subQ0}),-1.0]])]});}
            var Q5;
            {var subQ2=sQuery(id+"F20.wireOp",EDGE,"E92");Q5=makeQuery(id+"F20.imprint","IMPRINT",FACE,{"disambiguationData":[TD([[makeQuery(id+"F20.imprint","IMPRINT",EDGE,{"derivedFrom":subQ2}),-1.0]])]});}
            extrude(context, id + "F26", {"entities" : qUnion([Q0, Q1, Q2, Q3, Q4, Q5]), "operationType" : NewBodyOperationType.REMOVE, "depth" : 25 * mm, "offsetDistance" : 25 * mm});
        }
        {
            var Q0;
            {var subQ0=sQuery(id+"F20.wireOp",EDGE,"E82");Q0=makeQuery(id+"F20.imprint","IMPRINT",FACE,{"disambiguationData":[TD([[makeQuery(id+"F20.imprint","IMPRINT",EDGE,{"derivedFrom":subQ0}),-1.0]])]});}
            var Q1;
            {var subQ0=sQuery(id+"F20.wireOp",EDGE,"E80");Q1=makeQuery(id+"F20.imprint","IMPRINT",FACE,{"disambiguationData":[TD([[makeQuery(id+"F20.imprint","IMPRINT",EDGE,{"derivedFrom":subQ0}),-1.0]])]});}
            var Q2;
            {var subQ3=sQuery(id+"F20.wireOp",EDGE,"E67");Q2=makeQuery(id+"F20.imprint","IMPRINT",FACE,{"disambiguationData":[TD([[makeQuery(id+"F20.imprint","IMPRINT",EDGE,{"derivedFrom":subQ3}),1.0]])]});}
            var Q3;
            {var subQ3=sQuery(id+"F20.wireOp",EDGE,"E68");Q3=makeQuery(id+"F20.imprint","IMPRINT",FACE,{"disambiguationData":[TD([[makeQuery(id+"F20.imprint","IMPRINT",EDGE,{"derivedFrom":subQ3}),-1.0]])]});}
            var Q4;
            {var subQ2=sQuery(id+"F20.wireOp",EDGE,"E75");Q4=makeQuery(id+"F20.imprint","IMPRINT",FACE,{"disambiguationData":[TD([[makeQuery(id+"F20.imprint","IMPRINT",EDGE,{"derivedFrom":subQ2}),-1.0]])]});}
            var Q5;
            {var subQ0=sQuery(id+"F20.wireOp",EDGE,"E77");Q5=makeQuery(id+"F20.imprint","IMPRINT",FACE,{"disambiguationData":[TD([[makeQuery(id+"F20.imprint","IMPRINT",EDGE,{"derivedFrom":subQ0}),-1.0]])]});}
            extrude(context, id + "F27", {"entities" : qUnion([Q0, Q1, Q2, Q3, Q4, Q5]), "operationType" : NewBodyOperationType.ADD, "oppositeDirection" : true, "depth" : 25 * mm, "offsetDistance" : 25 * mm});
        }
        {
            var Q0;
            {var subQ0=sQuery(id+"F20.wireOp",EDGE,"E78");Q0=makeQuery(id+"F20.imprint","IMPRINT",FACE,{"disambiguationData":[TD([[makeQuery(id+"F20.imprint","IMPRINT",EDGE,{"derivedFrom":subQ0}),-1.0]])]});}
            var Q1;
            {var subQ0=sQuery(id+"F20.wireOp",EDGE,"E76");Q1=makeQuery(id+"F20.imprint","IMPRINT",FACE,{"disambiguationData":[TD([[makeQuery(id+"F20.imprint","IMPRINT",EDGE,{"derivedFrom":subQ0}),-1.0]])]});}
            var Q2;
            {var subQ0=sQuery(id+"F20.wireOp",EDGE,"E67");Q2=makeQuery(id+"F20.imprint","IMPRINT",FACE,{"disambiguationData":[TD([[makeQuery(id+"F20.imprint","IMPRINT",EDGE,{"derivedFrom":subQ0}),-1.0]])]});}
            var Q3;
            {var subQ0=sQuery(id+"F20.wireOp",EDGE,"E68");Q3=makeQuery(id+"F20.imprint","IMPRINT",FACE,{"disambiguationData":[TD([[makeQuery(id+"F20.imprint","IMPRINT",EDGE,{"derivedFrom":subQ0}),1.0]])]});}
            var Q4;
            {var subQ0=sQuery(id+"F20.wireOp",EDGE,"E81");Q4=makeQuery(id+"F20.imprint","IMPRINT",FACE,{"disambiguationData":[TD([[makeQuery(id+"F20.imprint","IMPRINT",EDGE,{"derivedFrom":subQ0}),-1.0]])]});}
            var Q5;
            {var subQ0=sQuery(id+"F20.wireOp",EDGE,"E83");Q5=makeQuery(id+"F20.imprint","IMPRINT",FACE,{"disambiguationData":[TD([[makeQuery(id+"F20.imprint","IMPRINT",EDGE,{"derivedFrom":subQ0}),1.0]])]});}
            extrude(context, id + "F28", {"entities" : qUnion([Q0, Q1, Q2, Q3, Q4, Q5]), "operationType" : NewBodyOperationType.REMOVE, "depth" : 25 * mm, "offsetDistance" : 25 * mm});
        }
    });
